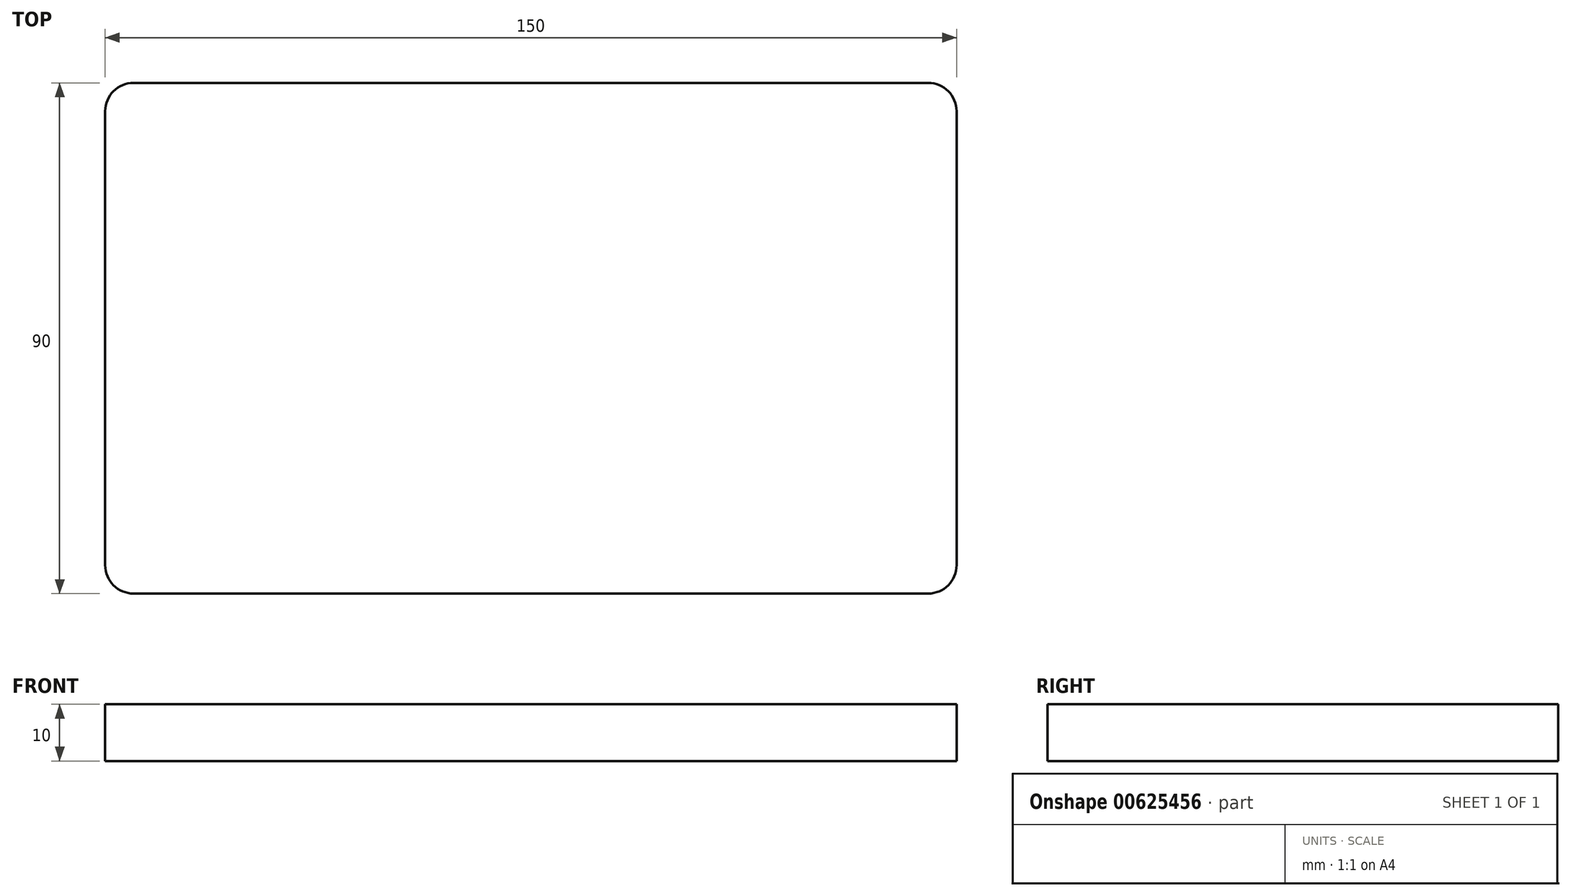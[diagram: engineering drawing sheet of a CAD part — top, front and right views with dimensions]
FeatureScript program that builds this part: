
annotation { "Feature Type Name" : "Feature", "Feature Type Description" : "" }
export const myFeature = defineFeature(function(context is Context, id is Id, definition is map)
    precondition{}
    {
        {
            var Q0;
            Q0=qCreatedBy(makeId("Top.planeOp"),FACE);
            var sketch = newSketch(context, id + "F0", { "sketchPlane" : qUnion([Q0])});
            skLineSegment(sketch, "E0.bottom", {"start": v(-70, 45) * mm, "end": v(70, 45) * mm});
            skLineSegment(sketch, "E0.top", {"start": v(-70, -45) * mm, "end": v(70, -45) * mm});
            skLineSegment(sketch, "E0.left", {"start": v(-75, 40) * mm, "end": v(-75, -40) * mm});
            skLineSegment(sketch, "E0.right", {"start": v(75, 40) * mm, "end": v(75, -40) * mm});
            skPoint(sketch, "E0.middle", {"position": v(0, 0) * mm});
            skPoint(sketch, "E1.visualSharp", {"position": v(-75, 45) * mm});
            skArc(sketch, "E1.filletArc", {"start": v(-70, 45) * mm, "mid": v(-73.54, 43.54) * mm, "end": v(-75, 40) * mm});
            skPoint(sketch, "E2.visualSharp", {"position": v(75, 45) * mm});
            skArc(sketch, "E2.filletArc", {"start": v(75, 40) * mm, "mid": v(73.54, 43.54) * mm, "end": v(70, 45) * mm});
            skPoint(sketch, "E3.visualSharp", {"position": v(75, -45) * mm});
            skArc(sketch, "E3.filletArc", {"start": v(70, -45) * mm, "mid": v(73.54, -43.54) * mm, "end": v(75, -40) * mm});
            skPoint(sketch, "E4.visualSharp", {"position": v(-75, -45) * mm});
            skArc(sketch, "E4.filletArc", {"start": v(-75, -40) * mm, "mid": v(-73.54, -43.54) * mm, "end": v(-70, -45) * mm});
            skSolve(sketch);
        }
        {
            var Q0;
            Q0 = qSketchRegion(id + "F0", true);
            extrude(context, id + "F1", {"entities" : qUnion([Q0]), "depth" : 10 * mm, "offsetDistance" : 25 * mm});
        }
    });
